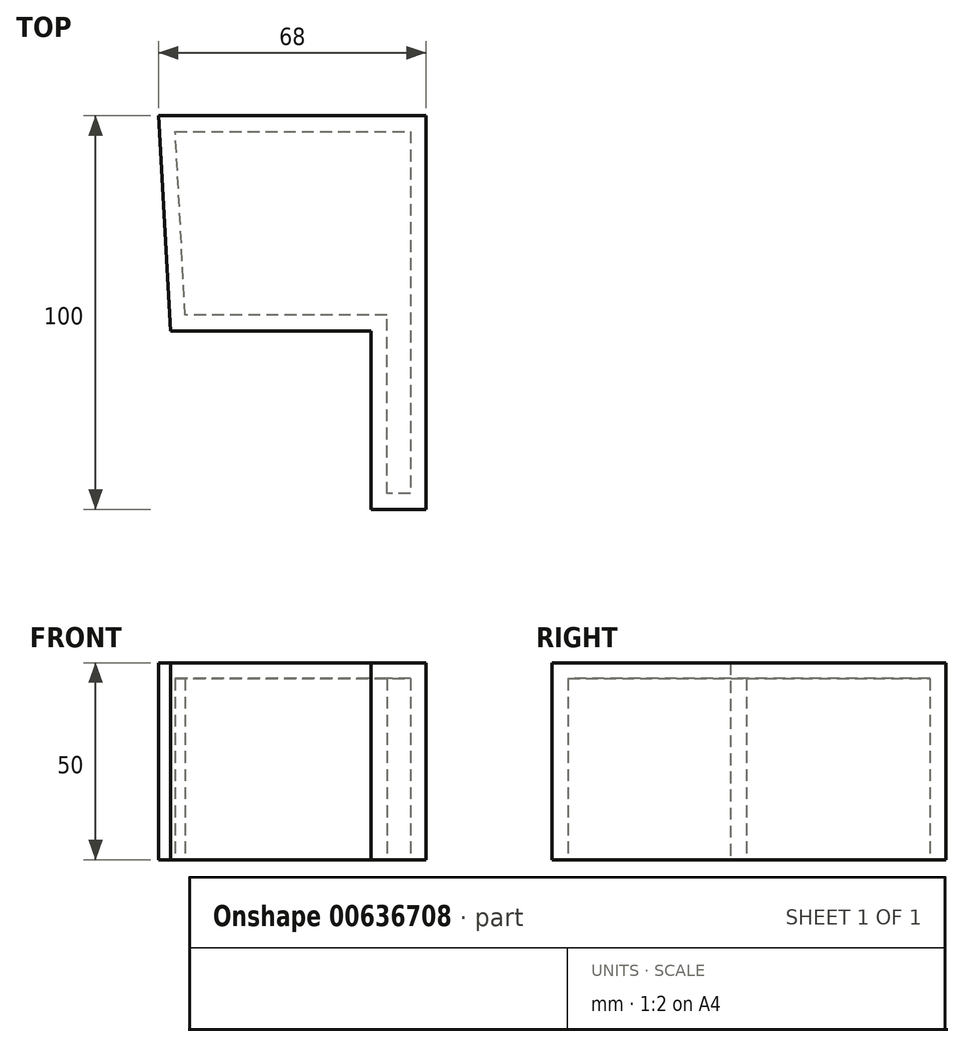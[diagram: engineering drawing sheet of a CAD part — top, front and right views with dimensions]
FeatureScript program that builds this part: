
annotation { "Feature Type Name" : "Feature", "Feature Type Description" : "" }
export const myFeature = defineFeature(function(context is Context, id is Id, definition is map)
    precondition{}
    {
        {
            var Q0;
            Q0=qCreatedBy(makeId("Top.planeOp"),FACE);
            var sketch = newSketch(context, id + "F0", { "sketchPlane" : qUnion([Q0])});
            skLineSegment(sketch, "E0", {"start": v(-29, 0) * mm, "end": v(-32, 54.65) * mm});
            skLineSegment(sketch, "E1", {"start": v(-32, 54.65) * mm, "end": v(36, 54.65) * mm});
            skLineSegment(sketch, "E2", {"start": v(36, 54.65) * mm, "end": v(36, -45.35) * mm});
            skLineSegment(sketch, "E3", {"start": v(36, -45.35) * mm, "end": v(22, -45.35) * mm});
            skLineSegment(sketch, "E4", {"start": v(22, -45.35) * mm, "end": v(22, 0) * mm});
            skLineSegment(sketch, "E5", {"start": v(22, 0) * mm, "end": v(-29, 0) * mm});
            skSolve(sketch);
        }
        {
            var Q0;
            Q0 = qSketchRegion(id + "F0", true);
            extrude(context, id + "F1", {"entities" : qUnion([Q0]), "depth" : 50 * mm, "offsetDistance" : 25 * mm});
        }
        {
            var Q0;
            Q0=makeQuery(id+"F1.opExtrude","CAP_FACE",FACE,{"disambiguationData":[OSD([sQuery(id+"F0.wireOp",EDGE,"E0"),sQuery(id+"F0.wireOp",EDGE,"E1"),sQuery(id+"F0.wireOp",EDGE,"E2"),sQuery(id+"F0.wireOp",EDGE,"E3"),sQuery(id+"F0.wireOp",EDGE,"E4"),sQuery(id+"F0.wireOp",EDGE,"E5")])],"isStart":true});
            shell(context, id + "F2", {"entities" : qUnion([Q0]), "thickness" : 4 * mm});
        }
    });
